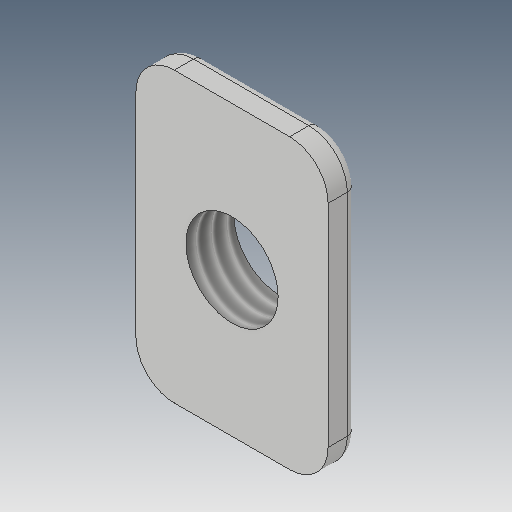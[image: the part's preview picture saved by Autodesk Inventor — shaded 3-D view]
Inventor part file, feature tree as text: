
AUTODESK INVENTOR PART (.ipt)
format: ipt  version: 2017 (Build 210142000, 142)  size: 159,744 bytes
history: native  units: mm
features: other x3, sketch x2
ambient origin geometry x8: Origin, YZ Plane, XZ Plane, XY Plane, X Axis, Y Axis, Z Axis, Center Point
bodies: Solid1 (feature_tree)
feature tree (5):
  other  "M5 Tee Nut-Generic.ipt"
  other  "Solid1::M5 Tee Nut-Generic.ipt"
  other  "TaggingFeature1"
  sketch  "Sketch1"  dims[d0=10.0mm]
  sketch  "Sketch2"
